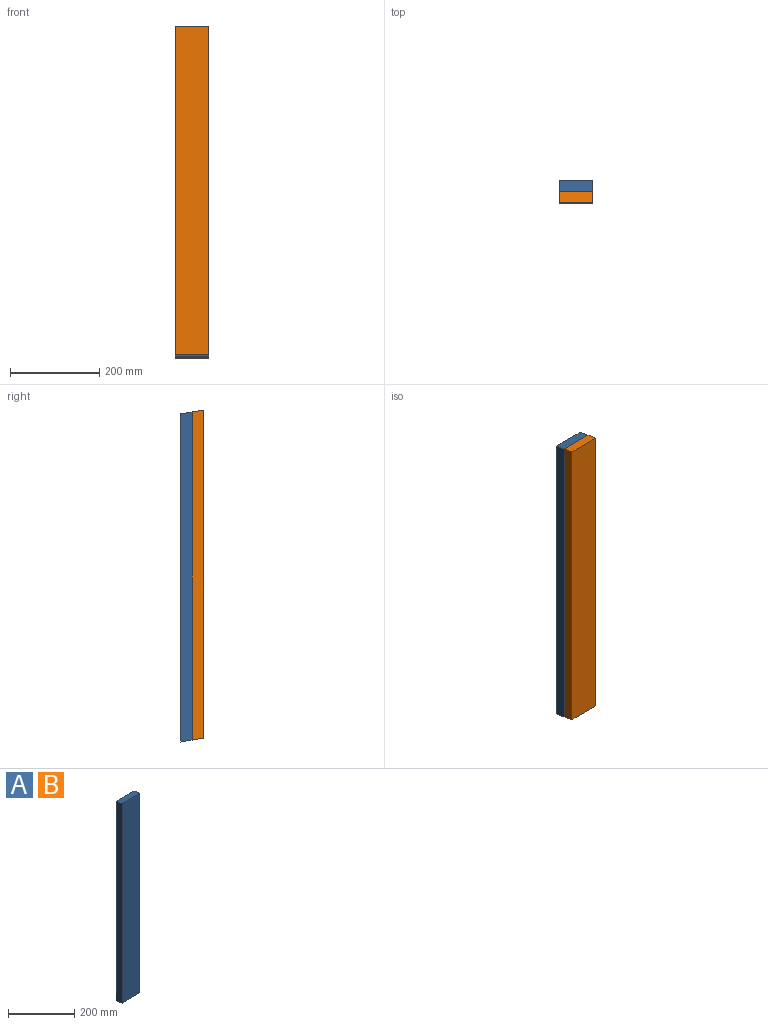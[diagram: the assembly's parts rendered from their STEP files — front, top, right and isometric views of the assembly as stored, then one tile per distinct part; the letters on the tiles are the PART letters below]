
ASSEMBLY  parts=2 mates=1
PART A: 6 faces, bbox 76x25x740 mm
  f0: plane 735.59x76mm, normal (0,1,0), area 55905mm2, adj f1,f2,f4,f5
  f1: plane 740x25mm, normal (1,0,0), area 18389.8mm2, adj f0,f3,f4,f5
  f2: plane 740x25mm, normal (-1,0,0), area 18389.8mm2, adj f0,f3,f4,f5
  f3: plane 735.59x76mm, normal (0,-1,0), area 55905mm2, adj f1,f2,f4,f5
  f4: plane 76x25mm, normal (0,-0.17,-0.98), area 1929.3mm2, adj f0,f1,f2,f3
  f5: plane 76x25mm, normal (0,0.17,0.98), area 1929.3mm2, adj f0,f1,f2,f3
PART B: same geometry as A
PLACE A t=(47.4,13.78,53.12)mm
PLACE B t=(47.4,-11.22,57.53)mm
MATE fastened B.f0 <-> A.f3  axis (0,1,0) through (16.56,-11.22,414.18)mm
